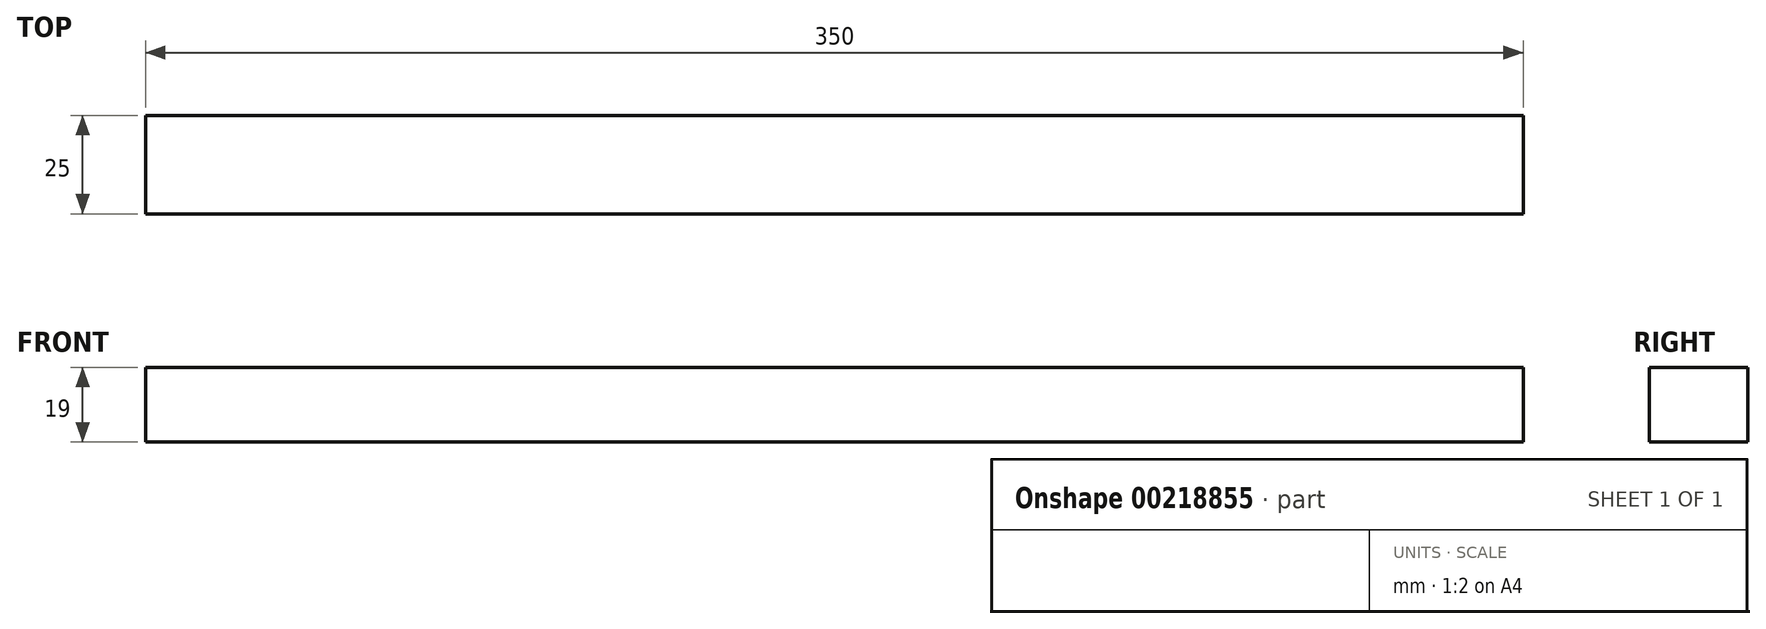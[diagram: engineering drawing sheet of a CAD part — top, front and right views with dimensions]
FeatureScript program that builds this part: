
annotation { "Feature Type Name" : "Feature", "Feature Type Description" : "" }
export const myFeature = defineFeature(function(context is Context, id is Id, definition is map)
    precondition{}
    {
        {
            var Q0;
            Q0=qCreatedBy(makeId("Front.planeOp"),FACE);
            var sketch = newSketch(context, id + "F0", { "sketchPlane" : qUnion([Q0])});
            skLineSegment(sketch, "E0.bottom", {"start": v(-139.57, 19) * mm, "end": v(210.43, 19) * mm});
            skLineSegment(sketch, "E0.top", {"start": v(-139.57, 0) * mm, "end": v(210.43, 0) * mm});
            skLineSegment(sketch, "E0.left", {"start": v(-139.57, 19) * mm, "end": v(-139.57, 0) * mm});
            skLineSegment(sketch, "E0.right", {"start": v(210.43, 19) * mm, "end": v(210.43, 0) * mm});
            skSolve(sketch);
        }
        {
            var Q0;
            Q0=makeQuery(id+"F0.imprint","IMPRINT",FACE,{"disambiguationData":[TD([[makeQuery(id+"F0.imprint","IMPRINT",EDGE,{"derivedFrom":sQuery(id+"F0.wireOp",EDGE,"E0.bottom")}),-1.0]])]});
            extrude(context, id + "F1", {"entities" : qUnion([Q0]), "depth" : 25 * mm});
        }
    });
